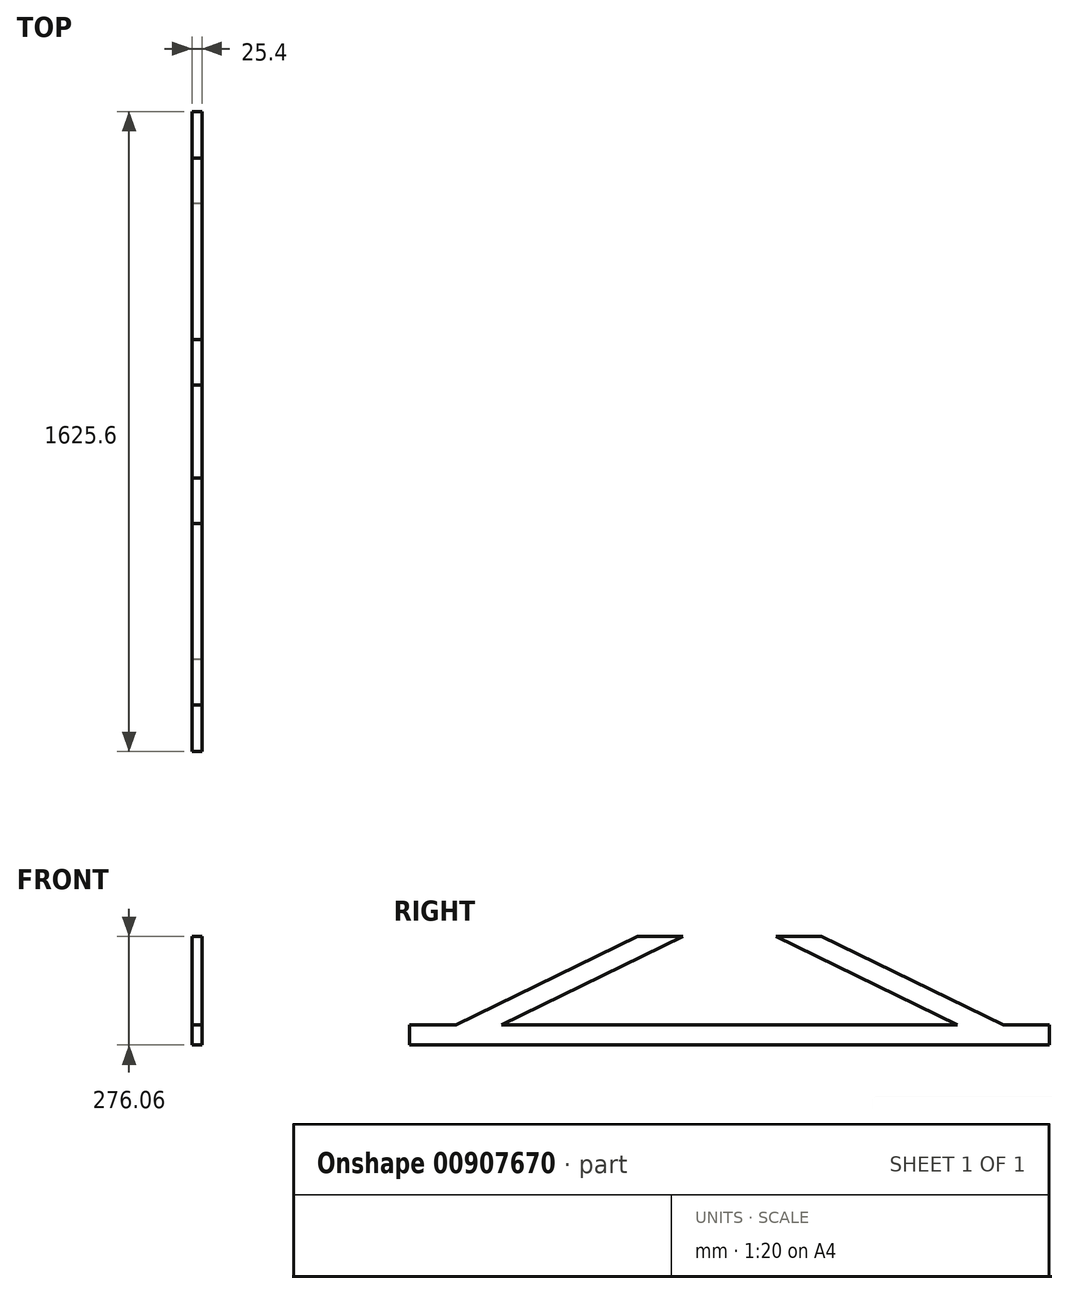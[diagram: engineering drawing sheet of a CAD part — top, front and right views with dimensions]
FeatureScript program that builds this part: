
annotation { "Feature Type Name" : "Feature", "Feature Type Description" : "" }
export const myFeature = defineFeature(function(context is Context, id is Id, definition is map)
    precondition{}
    {
        {
            var Q0;
            Q0=qCreatedBy(makeId("Right.planeOp"),FACE);
            var sketch = newSketch(context, id + "F0", { "sketchPlane" : qUnion([Q0])});
            skLineSegment(sketch, "E0.bottom", {"start": v(812.8, 163.43) * mm, "end": v(-812.8, 163.43) * mm});
            skLineSegment(sketch, "E0.top", {"start": v(812.8, -163.43) * mm, "end": v(-812.8, -163.43) * mm});
            skLineSegment(sketch, "E0.left", {"start": v(812.8, 163.43) * mm, "end": v(812.8, 112.63) * mm});
            skLineSegment(sketch, "E0.right", {"start": v(-812.8, 163.43) * mm, "end": v(-812.8, 112.63) * mm});
            skPoint(sketch, "E0.middle", {"position": v(0, 0) * mm});
            skLineSegment(sketch, "E1.bottom", {"start": v(-812.8, 163.43) * mm, "end": v(812.8, 163.43) * mm});
            skLineSegment(sketch, "E1.top", {"start": v(-812.8, 112.63) * mm, "end": v(812.8, 112.63) * mm});
            skLineSegment(sketch, "E2.top", {"start": v(579.44, -112.63) * mm, "end": v(-812.8, -112.63) * mm});
            skLineSegment(sketch, "E2.left", {"start": v(812.8, -163.43) * mm, "end": v(812.8, -112.63) * mm});
            skLineSegment(sketch, "E2.right", {"start": v(-812.8, -163.43) * mm, "end": v(-812.8, -112.63) * mm});
            skLineSegment(sketch, "E3.trimOffspring", {"start": v(812.8, -112.63) * mm, "end": v(812.8, -163.43) * mm});
            skLineSegment(sketch, "E4.trimOffspring", {"start": v(-812.8, -112.63) * mm, "end": v(-812.8, -163.43) * mm});
            skLineSegment(sketch, "E5.bottom", {"start": v(579.44, 112.63) * mm, "end": v(-579.44, 112.63) * mm});
            skLineSegment(sketch, "E5.top", {"start": v(579.44, -112.63) * mm, "end": v(-579.44, -112.63) * mm});
            skLineSegment(sketch, "E6.bottom", {"start": v(118.26, 112.63) * mm, "end": v(-118.26, 112.63) * mm});
            skLineSegment(sketch, "E6.top", {"start": v(118.26, -112.63) * mm, "end": v(-118.26, -112.63) * mm});
            skLineSegment(sketch, "E7", {"start": v(579.44, -112.63) * mm, "end": v(118.26, 112.63) * mm});
            skLineSegment(sketch, "E8", {"start": v(-579.44, -112.63) * mm, "end": v(-118.26, 112.63) * mm});
            skPoint(sketch, "E9.start.orphan", {"position": v(348.85, 0) * mm});
            skLineSegment(sketch, "E10", {"start": v(579.44, -56.1) * mm, "end": v(234, 112.63) * mm});
            skLineSegment(sketch, "E11", {"start": v(579.44, -112.63) * mm, "end": v(812.8, -112.63) * mm});
            skLineSegment(sketch, "E12", {"start": v(234, 112.63) * mm, "end": v(695.18, -112.63) * mm});
            skLineSegment(sketch, "E13", {"start": v(-371.15, 45.65) * mm, "end": v(-695.18, -112.63) * mm});
            skLineSegment(sketch, "E14", {"start": v(-695.18, -112.63) * mm, "end": v(-371.15, 45.65) * mm});
            skLineSegment(sketch, "E15", {"start": v(-371.15, 45.65) * mm, "end": v(-234, 112.63) * mm});
            skPoint(sketch, "E16.start.orphan", {"position": v(-348.85, 0) * mm});
            skSolve(sketch);
        }
        {
            var Q0;
            Q0=makeQuery(id+"F0.imprint","IMPRINT",FACE,{"disambiguationData":[TD([[makeQuery(id+"F0.imprint","IMPRINT",EDGE,{"derivedFrom":sQuery(id+"F0.wireOp",EDGE,"E1.bottom")}),-1.0]])]});
            var Q1;
            {var subQ1=sQuery(id+"F0.wireOp",EDGE,"E8");Q1=makeQuery(id+"F0.imprint","IMPRINT",FACE,{"disambiguationData":[TD([[makeQuery(id+"F0.imprint","IMPRINT",EDGE,{"derivedFrom":subQ1}),1.0]])]});}
            var Q2;
            {var subQ0=sQuery(id+"F0.wireOp",EDGE,"E7");Q2=makeQuery(id+"F0.imprint","IMPRINT",FACE,{"disambiguationData":[TD([[makeQuery(id+"F0.imprint","IMPRINT",EDGE,{"derivedFrom":subQ0}),-1.0]])]});}
            var Q3;
            Q3=makeQuery(id+"F0.imprint","IMPRINT",FACE,{"disambiguationData":[TD([[makeQuery(id+"F0.imprint","IMPRINT",EDGE,{"derivedFrom":sQuery(id+"F0.wireOp",EDGE,"E0.top")}),-1.0]])]});
            extrude(context, id + "F1", {"entities" : qUnion([Q0, Q1, Q2, Q3]), "depth" : 25.4 * mm, "offsetDistance" : 25.4 * mm});
        }
    });
